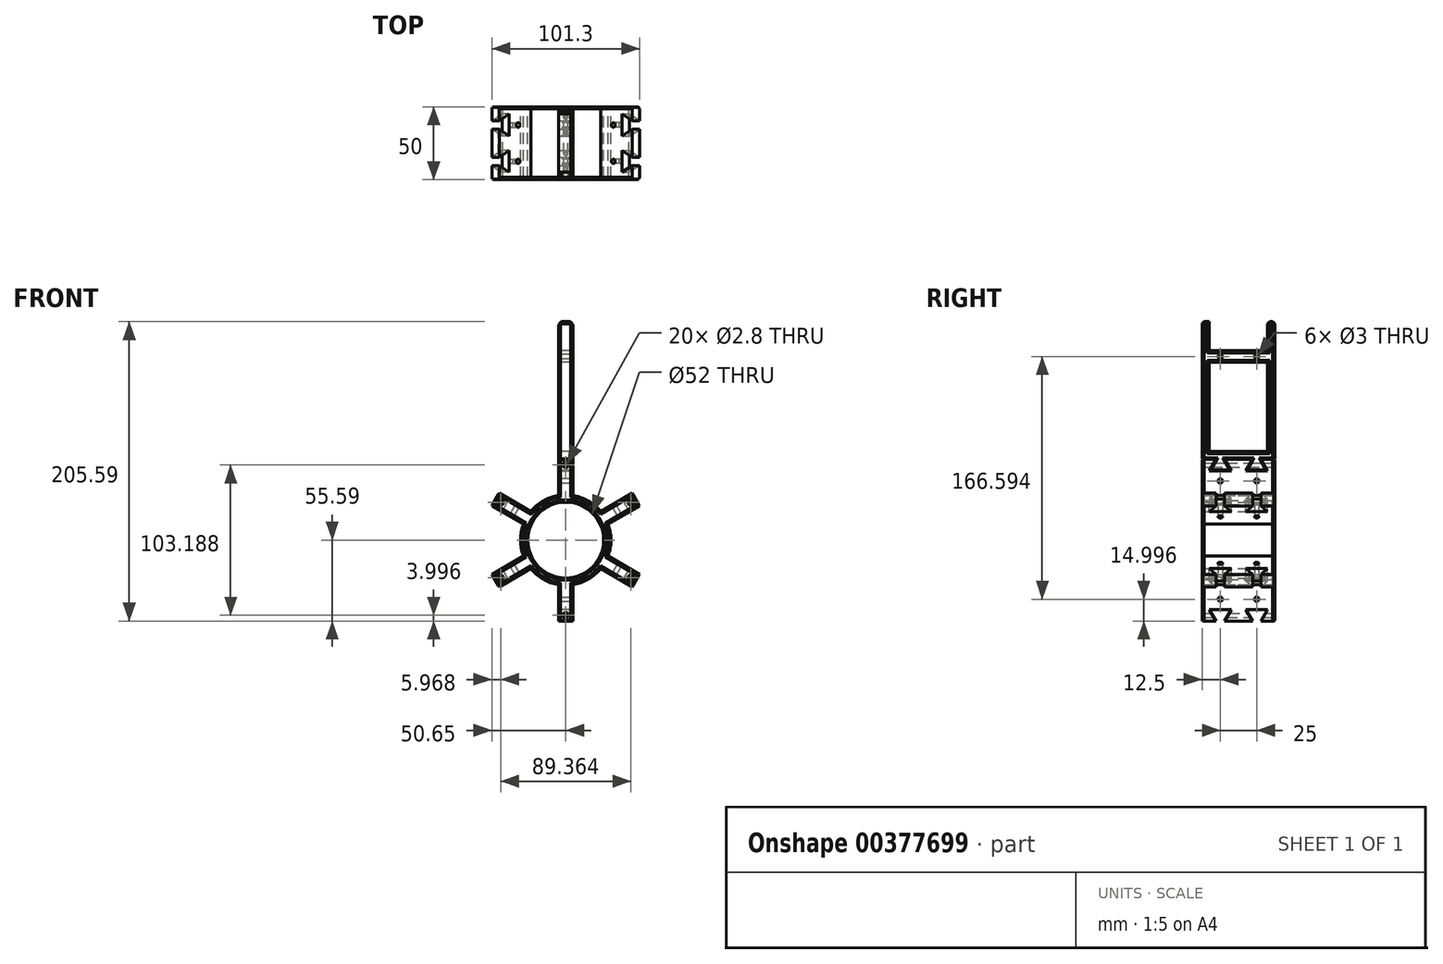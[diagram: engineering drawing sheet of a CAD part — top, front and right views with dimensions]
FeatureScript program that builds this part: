
annotation { "Feature Type Name" : "Feature", "Feature Type Description" : "" }
export const myFeature = defineFeature(function(context is Context, id is Id, definition is map)
    precondition{}
    {
        {
            var Q0;
            Q0=qCreatedBy(makeId("Front.planeOp"),FACE);
            var sketch = newSketch(context, id + "F0", { "sketchPlane" : qUnion([Q0])});
            skCircle(sketch, "E0", {"center": v(0, 0) * mm, "radius": 26 * mm});
            skCircle(sketch, "E1", {"center": v(0, 0) * mm, "radius": 31 * mm});
            skSolve(sketch);
        }
        {
            var Q0;
            Q0=makeQuery(id+"F0.imprint","IMPRINT",FACE,{"disambiguationData":[TD([[makeQuery(id+"F0.imprint","IMPRINT",EDGE,{"derivedFrom":sQuery(id+"F0.wireOp",EDGE,"E0")}),-1.0]])]});
            extrude(context, id + "F1", {"entities" : qUnion([Q0]), "depth" : 50 * mm});
        }
        {
            var Q0;
            Q0=makeQuery(id+"F1.opExtrude","CAP_FACE",FACE,{"disambiguationData":[OSD([sQuery(id+"F0.wireOp",EDGE,"E0"),sQuery(id+"F0.wireOp",EDGE,"E1")])],"isStart":true});
            var sketch = newSketch(context, id + "F2", { "sketchPlane" : qUnion([Q0])});
            skLineSegment(sketch, "E2.bottom", {"start": v(-5, 30.6) * mm, "end": v(5, 30.6) * mm});
            skLineSegment(sketch, "E2.top", {"start": v(-5, 55.6) * mm, "end": v(5, 55.6) * mm});
            skLineSegment(sketch, "E2.left", {"start": v(-5, 30.6) * mm, "end": v(-5, 55.6) * mm});
            skLineSegment(sketch, "E2.right", {"start": v(5, 30.6) * mm, "end": v(5, 55.6) * mm});
            skSolve(sketch);
        }
        {
            var Q0;
            Q0=makeQuery(id+"F2.imprint","IMPRINT",FACE,{"disambiguationData":[TD([[makeQuery(id+"F2.imprint","IMPRINT",EDGE,{"derivedFrom":sQuery(id+"F2.wireOp",EDGE,"E2.top")}),-1.0]])]});
            extrude(context, id + "F3", {"entities" : qUnion([Q0]), "operationType" : NewBodyOperationType.ADD, "oppositeDirection" : true, "depth" : 50 * mm});
        }
        {
            var Q0;
            Q0=makeQuery(id+"F3.opExtrude","SWEPT_FACE",FACE,{"disambiguationData":[OSD([sQuery(id+"F2.wireOp",EDGE,"E2.left")])]});
            var sketch = newSketch(context, id + "F4", { "sketchPlane" : qUnion([Q0])});
            skLineSegment(sketch, "E3", {"start": v(-40.38, 55.6) * mm, "end": v(-45, 47.6) * mm});
            skLineSegment(sketch, "E4", {"start": v(-45, 47.6) * mm, "end": v(-30, 47.6) * mm});
            skLineSegment(sketch, "E5", {"start": v(-30, 47.6) * mm, "end": v(-34.62, 55.6) * mm});
            skLineSegment(sketch, "E6", {"start": v(-9.62, 55.6) * mm, "end": v(-5, 47.6) * mm});
            skLineSegment(sketch, "E7", {"start": v(-5, 47.6) * mm, "end": v(-20, 47.6) * mm});
            skLineSegment(sketch, "E8", {"start": v(-20, 47.6) * mm, "end": v(-15.38, 55.6) * mm});
            skLineSegment(sketch, "E9", {"start": v(-40.38, 55.6) * mm, "end": v(-34.62, 55.6) * mm});
            skLineSegment(sketch, "E10", {"start": v(-15.38, 55.6) * mm, "end": v(-9.62, 55.6) * mm});
            skSolve(sketch);
        }
        {
            var Q0;
            Q0=makeQuery(id+"F4.imprint","IMPRINT",FACE,{"disambiguationData":[TD([[makeQuery(id+"F4.imprint","IMPRINT",EDGE,{"derivedFrom":sQuery(id+"F4.wireOp",EDGE,"E3")}),1.0]])]});
            var Q1;
            Q1=makeQuery(id+"F4.imprint","IMPRINT",FACE,{"disambiguationData":[TD([[makeQuery(id+"F4.imprint","IMPRINT",EDGE,{"derivedFrom":sQuery(id+"F4.wireOp",EDGE,"E6")}),-1.0]])]});
            extrude(context, id + "F5", {"entities" : qUnion([Q0, Q1]), "operationType" : NewBodyOperationType.REMOVE, "oppositeDirection" : true, "depth" : 25 * mm});
        }
        {
            var Q0;
            {var subQ0=sQuery(id+"F0.wireOp",EDGE,"E1");Q0=makeQuery(id+"F3.boolean.opBoolean","MERGE",FACE,{"derivedFrom":[makeQuery(id+"F1.opExtrude","CAP_FACE",FACE,{"disambiguationData":[OSD([sQuery(id+"F0.wireOp",EDGE,"E0"),subQ0])],"isStart":true}),makeQuery(id+"F3.opExtrude","CAP_FACE",FACE,{"disambiguationData":[OSD([subQ0,sQuery(id+"F2.wireOp",EDGE,"E2.top"),sQuery(id+"F2.wireOp",EDGE,"E2.left"),sQuery(id+"F2.wireOp",EDGE,"E2.right")])],"isStart":true})]});}
            var sketch = newSketch(context, id + "F6", { "sketchPlane" : qUnion([Q0])});
            skArc(sketch, "E11.0.0", {"start": v(-5, 30.6) * mm, "mid": v(0, -31) * mm, "end": v(5, 30.6) * mm});
            skLineSegment(sketch, "E11.0.1", {"start": v(5, 30.6) * mm, "end": v(5, 55.6) * mm});
            skLineSegment(sketch, "E11.0.2", {"start": v(5, 55.6) * mm, "end": v(-5, 55.6) * mm});
            skLineSegment(sketch, "E11.0.3", {"start": v(-5, 55.6) * mm, "end": v(-5, 30.6) * mm});
            skCircle(sketch, "E12", {"center": v(0, 51.6) * mm, "radius": 1.4 * mm});
            skSolve(sketch);
        }
        {
            var Q0;
            Q0=makeQuery(id+"F6.imprint","IMPRINT",FACE,{"disambiguationData":[TD([[makeQuery(id+"F6.imprint","IMPRINT",EDGE,{"derivedFrom":sQuery(id+"F6.wireOp",EDGE,"E12")}),1.0]])]});
            extrude(context, id + "F7", {"entities" : qUnion([Q0]), "operationType" : NewBodyOperationType.REMOVE, "endBound" : BoundingType.THROUGH_ALL, "oppositeDirection" : true, "depth" : 25 * mm});
        }
        {
            var Q0;
            Q0=makeQuery(id+"F3.opExtrude","SWEPT_FACE",FACE,{"disambiguationData":[OSD([sQuery(id+"F2.wireOp",EDGE,"E2.right")])]});
            var sketch = newSketch(context, id + "F8", { "sketchPlane" : qUnion([Q0])});
            skCircle(sketch, "E13", {"center": v(12.5, 40.6) * mm, "radius": 1.5 * mm});
            skCircle(sketch, "E14", {"center": v(37.5, 40.6) * mm, "radius": 1.5 * mm});
            skSolve(sketch);
        }
        {
            var Q0;
            Q0=makeQuery(id+"F8.imprint","IMPRINT",FACE,{"disambiguationData":[TD([[makeQuery(id+"F8.imprint","IMPRINT",EDGE,{"derivedFrom":sQuery(id+"F8.wireOp",EDGE,"E13")}),1.0]])]});
            var Q1;
            Q1=makeQuery(id+"F8.imprint","IMPRINT",FACE,{"disambiguationData":[TD([[makeQuery(id+"F8.imprint","IMPRINT",EDGE,{"derivedFrom":sQuery(id+"F8.wireOp",EDGE,"E14")}),1.0]])]});
            extrude(context, id + "F9", {"entities" : qUnion([Q0, Q1]), "operationType" : NewBodyOperationType.REMOVE, "oppositeDirection" : true, "depth" : 25 * mm});
        }
        {
            var Q0;
            Q0=makeQuery(id+"F1.opExtrude","SWEPT_BODY",BODY,{"disambiguationData":[OSD([sQuery(id+"F0.wireOp",EDGE,"E0"),sQuery(id+"F0.wireOp",EDGE,"E1")])]});
            var Q1;
            Q1=makeQuery(id+"F1.opExtrude","CAP_EDGE",EDGE,{"disambiguationData":[OSD([sQuery(id+"F0.wireOp",EDGE,"E0")])],"isStart":false});
            circularPattern(context, id + "F10", {"operationType" : NewBodyOperationType.ADD, "entities" : qUnion([Q0]), "axis" : qUnion([Q1]), "angle" : 360 * degree, "instanceCount" : 6, "equalSpace" : true});
        }
        {
            var Q0;
            Q0=makeQuery(id+"F3.opExtrude","SWEPT_FACE",FACE,{"disambiguationData":[OSD([sQuery(id+"F2.wireOp",EDGE,"E2.right")])]});
            var sketch = newSketch(context, id + "F11", { "sketchPlane" : qUnion([Q0])});
            skLineSegment(sketch, "E15.bottom", {"start": v(0, 55.8) * mm, "end": v(50, 55.8) * mm});
            skLineSegment(sketch, "E15.top", {"start": v(0, 150) * mm, "end": v(50, 150) * mm});
            skLineSegment(sketch, "E15.left", {"start": v(0, 55.8) * mm, "end": v(0, 150) * mm});
            skLineSegment(sketch, "E15.right", {"start": v(50, 55.8) * mm, "end": v(50, 150) * mm});
            skLineSegment(sketch, "E16", {"start": v(9.97, 55.8) * mm, "end": v(5.35, 47.8) * mm});
            skLineSegment(sketch, "E17", {"start": v(5.35, 47.8) * mm, "end": v(19.65, 47.8) * mm});
            skLineSegment(sketch, "E18", {"start": v(19.65, 47.8) * mm, "end": v(15.03, 55.8) * mm});
            skLineSegment(sketch, "E19", {"start": v(34.97, 55.8) * mm, "end": v(30.35, 47.8) * mm});
            skLineSegment(sketch, "E20", {"start": v(30.35, 47.8) * mm, "end": v(44.65, 47.8) * mm});
            skLineSegment(sketch, "E21", {"start": v(44.65, 47.8) * mm, "end": v(40.03, 55.8) * mm});
            skSolve(sketch);
        }
        {
            var Q0;
            Q0=makeQuery(id+"F11.imprint","IMPRINT",FACE,{"disambiguationData":[TD([[makeQuery(id+"F11.imprint","IMPRINT",EDGE,{"derivedFrom":sQuery(id+"F11.wireOp",EDGE,"E15.top")}),-1.0]])]});
            var Q1;
            {var subQ0=sQuery(id+"F11.wireOp",EDGE,"E16");Q1=makeQuery(id+"F11.imprint","IMPRINT",FACE,{"disambiguationData":[TD([[makeQuery(id+"F11.imprint","IMPRINT",EDGE,{"derivedFrom":subQ0}),1.0]])]});}
            var Q2;
            {var subQ0=sQuery(id+"F11.wireOp",EDGE,"E19");Q2=makeQuery(id+"F11.imprint","IMPRINT",FACE,{"disambiguationData":[TD([[makeQuery(id+"F11.imprint","IMPRINT",EDGE,{"derivedFrom":subQ0}),1.0]])]});}
            extrude(context, id + "F12", {"entities" : qUnion([Q0, Q1, Q2]), "oppositeDirection" : true, "depth" : 10 * mm});
        }
        {
            var Q0;
            Q0=makeQuery(id+"F12.opExtrude","CAP_FACE",FACE,{"disambiguationData":[OSD([sQuery(id+"F11.wireOp",EDGE,"E15.bottom"),sQuery(id+"F11.wireOp",EDGE,"E15.top"),sQuery(id+"F11.wireOp",EDGE,"E15.left"),sQuery(id+"F11.wireOp",EDGE,"E15.right"),sQuery(id+"F11.wireOp",EDGE,"E16"),sQuery(id+"F11.wireOp",EDGE,"E17"),sQuery(id+"F11.wireOp",EDGE,"E18"),sQuery(id+"F11.wireOp",EDGE,"E19"),sQuery(id+"F11.wireOp",EDGE,"E20"),sQuery(id+"F11.wireOp",EDGE,"E21")])],"isStart":true});
            var sketch = newSketch(context, id + "F13", { "sketchPlane" : qUnion([Q0])});
            skLineSegment(sketch, "E22.bottom", {"start": v(5, 122) * mm, "end": v(45, 122) * mm});
            skLineSegment(sketch, "E22.top", {"start": v(5, 60.8) * mm, "end": v(45, 60.8) * mm});
            skLineSegment(sketch, "E22.left", {"start": v(5, 122) * mm, "end": v(5, 60.8) * mm});
            skLineSegment(sketch, "E22.right", {"start": v(45, 122) * mm, "end": v(45, 60.8) * mm});
            skLineSegment(sketch, "E23.bottom", {"start": v(5, 150) * mm, "end": v(45, 150) * mm});
            skLineSegment(sketch, "E23.top", {"start": v(5, 130) * mm, "end": v(45, 130) * mm});
            skLineSegment(sketch, "E23.left", {"start": v(5, 150) * mm, "end": v(5, 130) * mm});
            skLineSegment(sketch, "E23.right", {"start": v(45, 150) * mm, "end": v(45, 130) * mm});
            skCircle(sketch, "E24", {"center": v(12.5, 126) * mm, "radius": 1.5 * mm});
            skCircle(sketch, "E25", {"center": v(37.5, 126) * mm, "radius": 1.5 * mm});
            skSolve(sketch);
        }
        {
            var Q0;
            Q0=makeQuery(id+"F13.imprint","IMPRINT",FACE,{"disambiguationData":[TD([[makeQuery(id+"F13.imprint","IMPRINT",EDGE,{"derivedFrom":sQuery(id+"F13.wireOp",EDGE,"E23.bottom")}),-1.0]])]});
            var Q1;
            Q1=makeQuery(id+"F13.imprint","IMPRINT",FACE,{"disambiguationData":[TD([[makeQuery(id+"F13.imprint","IMPRINT",EDGE,{"derivedFrom":sQuery(id+"F13.wireOp",EDGE,"E22.bottom")}),-1.0]])]});
            var Q2;
            Q2=makeQuery(id+"F13.imprint","IMPRINT",FACE,{"disambiguationData":[TD([[makeQuery(id+"F13.imprint","IMPRINT",EDGE,{"derivedFrom":sQuery(id+"F13.wireOp",EDGE,"E24")}),1.0]])]});
            var Q3;
            Q3=makeQuery(id+"F13.imprint","IMPRINT",FACE,{"disambiguationData":[TD([[makeQuery(id+"F13.imprint","IMPRINT",EDGE,{"derivedFrom":sQuery(id+"F13.wireOp",EDGE,"E25")}),1.0]])]});
            extrude(context, id + "F14", {"entities" : qUnion([Q0, Q1, Q2, Q3]), "operationType" : NewBodyOperationType.REMOVE, "oppositeDirection" : true, "depth" : 25 * mm});
        }
        {
            var Q0;
            Q0=makeQuery(id+"F12.opExtrude","SWEPT_FACE",FACE,{"disambiguationData":[OSD([sQuery(id+"F11.wireOp",EDGE,"E15.left")])]});
            var sketch = newSketch(context, id + "F15", { "sketchPlane" : qUnion([Q0])});
            skCircle(sketch, "E26.0", {"center": v(0, 51.6) * mm, "radius": 1.4 * mm});
            skSolve(sketch);
        }
        {
            var Q0;
            Q0=makeQuery(id+"F15.imprint","IMPRINT",FACE,{"disambiguationData":[TD([[makeQuery(id+"F15.imprint","IMPRINT",EDGE,{"derivedFrom":sQuery(id+"F15.wireOp",EDGE,"E26.0")}),1.0]])]});
            extrude(context, id + "F16", {"entities" : qUnion([Q0]), "operationType" : NewBodyOperationType.REMOVE, "endBound" : BoundingType.THROUGH_ALL, "oppositeDirection" : true, "depth" : 25 * mm});
        }
        {
            assignVariable(context, id + "F17", {"name" : "c", "anyValue" : 1.5});
        }
        {
            var Q0;
            {var subQ0=sQuery(id+"F2.wireOp",EDGE,"E2.right");var subQ2=sQuery(id+"F0.wireOp",EDGE,"E1");Q0=makeQuery(id+"F10.boolean.opBoolean","SPLIT",EDGE,{"disambiguationData":[TD([makeQuery(id+"F3.opExtrude","SWEPT_FACE",FACE,{"disambiguationData":[OSD([subQ0])]})])],"derivedFrom":makeQuery(id+"F1.opExtrude","CAP_EDGE",EDGE,{"disambiguationData":[OSD([subQ2])],"isStart":false})});}
            var Q1;
            Q1=makeQuery(id+"F3.opExtrude","CAP_EDGE",EDGE,{"disambiguationData":[OSD([sQuery(id+"F2.wireOp",EDGE,"E2.right")])],"isStart":false});
            var Q2;
            Q2=makeQuery(id+"F3.opExtrude","CAP_EDGE",EDGE,{"disambiguationData":[OSD([sQuery(id+"F2.wireOp",EDGE,"E2.left")])],"isStart":false});
            var Q3;
            {var subQ0=sQuery(id+"F2.wireOp",EDGE,"E2.left");var subQ2=sQuery(id+"F0.wireOp",EDGE,"E1");Q3=makeQuery(id+"F10.boolean.opBoolean","SPLIT",EDGE,{"disambiguationData":[TD([makeQuery(id+"F3.opExtrude","SWEPT_FACE",FACE,{"disambiguationData":[OSD([subQ0])]})])],"derivedFrom":makeQuery(id+"F1.opExtrude","CAP_EDGE",EDGE,{"disambiguationData":[OSD([subQ2])],"isStart":false})});}
            var Q4;
            Q4=makeQuery(id+"F10.opPattern","COPY",EDGE,{"derivedFrom":makeQuery(id+"F3.opExtrude","CAP_EDGE",EDGE,{"disambiguationData":[OSD([sQuery(id+"F2.wireOp",EDGE,"E2.right")])],"isStart":false}),"instanceName":"5"});
            var Q5;
            Q5=makeQuery(id+"F10.opPattern","COPY",EDGE,{"derivedFrom":makeQuery(id+"F3.opExtrude","CAP_EDGE",EDGE,{"disambiguationData":[OSD([sQuery(id+"F2.wireOp",EDGE,"E2.left")])],"isStart":false}),"instanceName":"5"});
            var Q6;
            {var subQ0=sQuery(id+"F2.wireOp",EDGE,"E2.right");var subQ2=sQuery(id+"F0.wireOp",EDGE,"E1");Q6=makeQuery(id+"F10.boolean.opBoolean","SPLIT",EDGE,{"disambiguationData":[TD([makeQuery(id+"F10.opPattern","COPY",FACE,{"derivedFrom":makeQuery(id+"F3.opExtrude","SWEPT_FACE",FACE,{"disambiguationData":[OSD([subQ0])]}),"instanceName":"4"})])],"derivedFrom":makeQuery(id+"F1.opExtrude","CAP_EDGE",EDGE,{"disambiguationData":[OSD([subQ2])],"isStart":false})});}
            var Q7;
            Q7=makeQuery(id+"F10.opPattern","COPY",EDGE,{"derivedFrom":makeQuery(id+"F3.opExtrude","CAP_EDGE",EDGE,{"disambiguationData":[OSD([sQuery(id+"F2.wireOp",EDGE,"E2.right")])],"isStart":false}),"instanceName":"4"});
            var Q8;
            Q8=makeQuery(id+"F10.opPattern","COPY",EDGE,{"derivedFrom":makeQuery(id+"F3.opExtrude","CAP_EDGE",EDGE,{"disambiguationData":[OSD([sQuery(id+"F2.wireOp",EDGE,"E2.left")])],"isStart":false}),"instanceName":"4"});
            var Q9;
            {var subQ0=sQuery(id+"F2.wireOp",EDGE,"E2.right");var subQ2=sQuery(id+"F0.wireOp",EDGE,"E1");Q9=makeQuery(id+"F10.boolean.opBoolean","SPLIT",EDGE,{"disambiguationData":[TD([makeQuery(id+"F10.opPattern","COPY",FACE,{"derivedFrom":makeQuery(id+"F3.opExtrude","SWEPT_FACE",FACE,{"disambiguationData":[OSD([subQ0])]}),"instanceName":"3"})])],"derivedFrom":makeQuery(id+"F1.opExtrude","CAP_EDGE",EDGE,{"disambiguationData":[OSD([subQ2])],"isStart":false})});}
            var Q10;
            Q10=makeQuery(id+"F10.opPattern","COPY",EDGE,{"derivedFrom":makeQuery(id+"F3.opExtrude","CAP_EDGE",EDGE,{"disambiguationData":[OSD([sQuery(id+"F2.wireOp",EDGE,"E2.right")])],"isStart":false}),"instanceName":"3"});
            var Q11;
            Q11=makeQuery(id+"F10.opPattern","COPY",EDGE,{"derivedFrom":makeQuery(id+"F3.opExtrude","CAP_EDGE",EDGE,{"disambiguationData":[OSD([sQuery(id+"F2.wireOp",EDGE,"E2.left")])],"isStart":false}),"instanceName":"3"});
            var Q12;
            {var subQ0=sQuery(id+"F2.wireOp",EDGE,"E2.right");var subQ2=sQuery(id+"F0.wireOp",EDGE,"E1");Q12=makeQuery(id+"F10.boolean.opBoolean","SPLIT",EDGE,{"disambiguationData":[TD([makeQuery(id+"F10.opPattern","COPY",FACE,{"derivedFrom":makeQuery(id+"F3.opExtrude","SWEPT_FACE",FACE,{"disambiguationData":[OSD([subQ0])]}),"instanceName":"2"})])],"derivedFrom":makeQuery(id+"F1.opExtrude","CAP_EDGE",EDGE,{"disambiguationData":[OSD([subQ2])],"isStart":false})});}
            var Q13;
            Q13=makeQuery(id+"F10.opPattern","COPY",EDGE,{"derivedFrom":makeQuery(id+"F3.opExtrude","CAP_EDGE",EDGE,{"disambiguationData":[OSD([sQuery(id+"F2.wireOp",EDGE,"E2.right")])],"isStart":false}),"instanceName":"2"});
            var Q14;
            Q14=makeQuery(id+"F10.opPattern","COPY",EDGE,{"derivedFrom":makeQuery(id+"F3.opExtrude","CAP_EDGE",EDGE,{"disambiguationData":[OSD([sQuery(id+"F2.wireOp",EDGE,"E2.left")])],"isStart":false}),"instanceName":"2"});
            var Q15;
            {var subQ0=sQuery(id+"F2.wireOp",EDGE,"E2.right");var subQ2=sQuery(id+"F0.wireOp",EDGE,"E1");Q15=makeQuery(id+"F10.boolean.opBoolean","SPLIT",EDGE,{"disambiguationData":[TD([makeQuery(id+"F10.opPattern","COPY",FACE,{"derivedFrom":makeQuery(id+"F3.opExtrude","SWEPT_FACE",FACE,{"disambiguationData":[OSD([subQ0])]}),"instanceName":"1"})])],"derivedFrom":makeQuery(id+"F1.opExtrude","CAP_EDGE",EDGE,{"disambiguationData":[OSD([subQ2])],"isStart":false})});}
            var Q16;
            Q16=makeQuery(id+"F10.opPattern","COPY",EDGE,{"derivedFrom":makeQuery(id+"F3.opExtrude","CAP_EDGE",EDGE,{"disambiguationData":[OSD([sQuery(id+"F2.wireOp",EDGE,"E2.right")])],"isStart":false}),"instanceName":"1"});
            var Q17;
            Q17=makeQuery(id+"F10.opPattern","COPY",EDGE,{"derivedFrom":makeQuery(id+"F3.opExtrude","CAP_EDGE",EDGE,{"disambiguationData":[OSD([sQuery(id+"F2.wireOp",EDGE,"E2.left")])],"isStart":false}),"instanceName":"1"});
            var Q18;
            Q18=makeQuery(id+"F1.opExtrude","CAP_EDGE",EDGE,{"disambiguationData":[OSD([sQuery(id+"F0.wireOp",EDGE,"E0")])],"isStart":false});
            chamfer(context, id + "F18", {"entities" : qUnion([Q0, Q1, Q2, Q3, Q4, Q5, Q6, Q7, Q8, Q9, Q10, Q11, Q12, Q13, Q14, Q15, Q16, Q17, Q18]), "width" : (getVariable(context, 'c')) * mm, "tangentPropagation" : true});
        }
        {
            var Q0;
            Q0=makeQuery(id+"F10.opPattern","COPY",EDGE,{"derivedFrom":makeQuery(id+"F3.opExtrude","CAP_EDGE",EDGE,{"disambiguationData":[OSD([sQuery(id+"F2.wireOp",EDGE,"E2.right")])],"isStart":true}),"instanceName":"5"});
            var Q1;
            {var subQ1=sQuery(id+"F2.wireOp",EDGE,"E2.left");var subQ2=sQuery(id+"F0.wireOp",EDGE,"E1");Q1=makeQuery(id+"F10.boolean.opBoolean","SPLIT",EDGE,{"disambiguationData":[TD([makeQuery(id+"F3.opExtrude","SWEPT_FACE",FACE,{"disambiguationData":[OSD([subQ1])]})])],"derivedFrom":makeQuery(id+"F1.opExtrude","CAP_EDGE",EDGE,{"disambiguationData":[OSD([subQ2])],"isStart":true})});}
            var Q2;
            Q2=makeQuery(id+"F3.opExtrude","CAP_EDGE",EDGE,{"disambiguationData":[OSD([sQuery(id+"F2.wireOp",EDGE,"E2.left")])],"isStart":true});
            var Q3;
            Q3=makeQuery(id+"F3.opExtrude","CAP_EDGE",EDGE,{"disambiguationData":[OSD([sQuery(id+"F2.wireOp",EDGE,"E2.right")])],"isStart":true});
            var Q4;
            {var subQ0=sQuery(id+"F2.wireOp",EDGE,"E2.right");var subQ2=sQuery(id+"F0.wireOp",EDGE,"E1");Q4=makeQuery(id+"F10.boolean.opBoolean","SPLIT",EDGE,{"disambiguationData":[TD([makeQuery(id+"F3.opExtrude","SWEPT_FACE",FACE,{"disambiguationData":[OSD([subQ0])]})])],"derivedFrom":makeQuery(id+"F1.opExtrude","CAP_EDGE",EDGE,{"disambiguationData":[OSD([subQ2])],"isStart":true})});}
            var Q5;
            Q5=makeQuery(id+"F10.opPattern","COPY",EDGE,{"derivedFrom":makeQuery(id+"F3.opExtrude","CAP_EDGE",EDGE,{"disambiguationData":[OSD([sQuery(id+"F2.wireOp",EDGE,"E2.left")])],"isStart":true}),"instanceName":"1"});
            var Q6;
            Q6=makeQuery(id+"F10.opPattern","COPY",EDGE,{"derivedFrom":makeQuery(id+"F3.opExtrude","CAP_EDGE",EDGE,{"disambiguationData":[OSD([sQuery(id+"F2.wireOp",EDGE,"E2.right")])],"isStart":true}),"instanceName":"1"});
            var Q7;
            {var subQ0=sQuery(id+"F2.wireOp",EDGE,"E2.right");var subQ2=sQuery(id+"F0.wireOp",EDGE,"E1");Q7=makeQuery(id+"F10.boolean.opBoolean","SPLIT",EDGE,{"disambiguationData":[TD([makeQuery(id+"F10.opPattern","COPY",FACE,{"derivedFrom":makeQuery(id+"F3.opExtrude","SWEPT_FACE",FACE,{"disambiguationData":[OSD([subQ0])]}),"instanceName":"1"})])],"derivedFrom":makeQuery(id+"F1.opExtrude","CAP_EDGE",EDGE,{"disambiguationData":[OSD([subQ2])],"isStart":true})});}
            var Q8;
            Q8=makeQuery(id+"F10.opPattern","COPY",EDGE,{"derivedFrom":makeQuery(id+"F3.opExtrude","CAP_EDGE",EDGE,{"disambiguationData":[OSD([sQuery(id+"F2.wireOp",EDGE,"E2.left")])],"isStart":true}),"instanceName":"2"});
            var Q9;
            Q9=makeQuery(id+"F10.opPattern","COPY",EDGE,{"derivedFrom":makeQuery(id+"F3.opExtrude","CAP_EDGE",EDGE,{"disambiguationData":[OSD([sQuery(id+"F2.wireOp",EDGE,"E2.right")])],"isStart":true}),"instanceName":"2"});
            var Q10;
            Q10=makeQuery(id+"F10.opPattern","COPY",EDGE,{"derivedFrom":makeQuery(id+"F3.opExtrude","CAP_EDGE",EDGE,{"disambiguationData":[OSD([sQuery(id+"F2.wireOp",EDGE,"E2.left")])],"isStart":true}),"instanceName":"3"});
            var Q11;
            {var subQ0=sQuery(id+"F2.wireOp",EDGE,"E2.right");var subQ2=sQuery(id+"F0.wireOp",EDGE,"E1");Q11=makeQuery(id+"F10.boolean.opBoolean","SPLIT",EDGE,{"disambiguationData":[TD([makeQuery(id+"F10.opPattern","COPY",FACE,{"derivedFrom":makeQuery(id+"F3.opExtrude","SWEPT_FACE",FACE,{"disambiguationData":[OSD([subQ0])]}),"instanceName":"2"})])],"derivedFrom":makeQuery(id+"F1.opExtrude","CAP_EDGE",EDGE,{"disambiguationData":[OSD([subQ2])],"isStart":true})});}
            var Q12;
            Q12=makeQuery(id+"F10.opPattern","COPY",EDGE,{"derivedFrom":makeQuery(id+"F3.opExtrude","CAP_EDGE",EDGE,{"disambiguationData":[OSD([sQuery(id+"F2.wireOp",EDGE,"E2.right")])],"isStart":true}),"instanceName":"3"});
            var Q13;
            {var subQ0=sQuery(id+"F2.wireOp",EDGE,"E2.right");var subQ2=sQuery(id+"F0.wireOp",EDGE,"E1");Q13=makeQuery(id+"F10.boolean.opBoolean","SPLIT",EDGE,{"disambiguationData":[TD([makeQuery(id+"F10.opPattern","COPY",FACE,{"derivedFrom":makeQuery(id+"F3.opExtrude","SWEPT_FACE",FACE,{"disambiguationData":[OSD([subQ0])]}),"instanceName":"3"})])],"derivedFrom":makeQuery(id+"F1.opExtrude","CAP_EDGE",EDGE,{"disambiguationData":[OSD([subQ2])],"isStart":true})});}
            var Q14;
            Q14=makeQuery(id+"F10.opPattern","COPY",EDGE,{"derivedFrom":makeQuery(id+"F3.opExtrude","CAP_EDGE",EDGE,{"disambiguationData":[OSD([sQuery(id+"F2.wireOp",EDGE,"E2.left")])],"isStart":true}),"instanceName":"4"});
            var Q15;
            Q15=makeQuery(id+"F10.opPattern","COPY",EDGE,{"derivedFrom":makeQuery(id+"F3.opExtrude","CAP_EDGE",EDGE,{"disambiguationData":[OSD([sQuery(id+"F2.wireOp",EDGE,"E2.right")])],"isStart":true}),"instanceName":"4"});
            var Q16;
            {var subQ0=sQuery(id+"F2.wireOp",EDGE,"E2.right");var subQ2=sQuery(id+"F0.wireOp",EDGE,"E1");Q16=makeQuery(id+"F10.boolean.opBoolean","SPLIT",EDGE,{"disambiguationData":[TD([makeQuery(id+"F10.opPattern","COPY",FACE,{"derivedFrom":makeQuery(id+"F3.opExtrude","SWEPT_FACE",FACE,{"disambiguationData":[OSD([subQ0])]}),"instanceName":"4"})])],"derivedFrom":makeQuery(id+"F1.opExtrude","CAP_EDGE",EDGE,{"disambiguationData":[OSD([subQ2])],"isStart":true})});}
            var Q17;
            Q17=makeQuery(id+"F10.opPattern","COPY",EDGE,{"derivedFrom":makeQuery(id+"F3.opExtrude","CAP_EDGE",EDGE,{"disambiguationData":[OSD([sQuery(id+"F2.wireOp",EDGE,"E2.left")])],"isStart":true}),"instanceName":"5"});
            var Q18;
            Q18=makeQuery(id+"F1.opExtrude","CAP_EDGE",EDGE,{"disambiguationData":[OSD([sQuery(id+"F0.wireOp",EDGE,"E0")])],"isStart":true});
            chamfer(context, id + "F19", {"entities" : qUnion([Q0, Q1, Q2, Q3, Q4, Q5, Q6, Q7, Q8, Q9, Q10, Q11, Q12, Q13, Q14, Q15, Q16, Q17, Q18]), "width" : (getVariable(context, 'c')) * mm, "tangentPropagation" : true});
        }
        {
            var Q0;
            Q0=makeQuery(id+"F12.opExtrude","CAP_EDGE",EDGE,{"disambiguationData":[OSD([sQuery(id+"F11.wireOp",EDGE,"E15.left")])],"isStart":true});
            var Q1;
            Q1=makeQuery(id+"F14.boolean.opBoolean","COPY",EDGE,{"derivedFrom":makeQuery(id+"F14.opExtrude","CAP_EDGE",EDGE,{"disambiguationData":[OSD([sQuery(id+"F13.wireOp",EDGE,"E22.left")])],"isStart":true})});
            var Q2;
            Q2=makeQuery(id+"F14.boolean.opBoolean","COPY",EDGE,{"derivedFrom":makeQuery(id+"F14.opExtrude","CAP_EDGE",EDGE,{"disambiguationData":[OSD([sQuery(id+"F13.wireOp",EDGE,"E22.bottom")])],"isStart":true})});
            var Q3;
            Q3=makeQuery(id+"F14.boolean.opBoolean","COPY",EDGE,{"derivedFrom":makeQuery(id+"F14.opExtrude","CAP_EDGE",EDGE,{"disambiguationData":[OSD([sQuery(id+"F13.wireOp",EDGE,"E22.right")])],"isStart":true})});
            var Q4;
            Q4=makeQuery(id+"F14.boolean.opBoolean","COPY",EDGE,{"derivedFrom":makeQuery(id+"F14.opExtrude","CAP_EDGE",EDGE,{"disambiguationData":[OSD([sQuery(id+"F13.wireOp",EDGE,"E22.top")])],"isStart":true})});
            var Q5;
            Q5=makeQuery(id+"F14.boolean.opBoolean","COPY",EDGE,{"derivedFrom":makeQuery(id+"F14.opExtrude","CAP_EDGE",EDGE,{"disambiguationData":[OSD([sQuery(id+"F13.wireOp",EDGE,"E23.top")])],"isStart":true})});
            var Q6;
            Q6=makeQuery(id+"F14.boolean.opBoolean","COPY",EDGE,{"derivedFrom":makeQuery(id+"F14.opExtrude","CAP_EDGE",EDGE,{"disambiguationData":[OSD([sQuery(id+"F13.wireOp",EDGE,"E23.left")])],"isStart":true})});
            var Q7;
            Q7=makeQuery(id+"F14.boolean.opBoolean","COPY",EDGE,{"derivedFrom":makeQuery(id+"F14.opExtrude","CAP_EDGE",EDGE,{"disambiguationData":[OSD([sQuery(id+"F13.wireOp",EDGE,"E23.right")])],"isStart":true})});
            var Q8;
            Q8=makeQuery(id+"F12.opExtrude","CAP_EDGE",EDGE,{"disambiguationData":[OSD([sQuery(id+"F11.wireOp",EDGE,"E15.right")])],"isStart":false});
            var Q9;
            Q9=makeQuery(id+"F12.opExtrude","CAP_EDGE",EDGE,{"disambiguationData":[OSD([sQuery(id+"F11.wireOp",EDGE,"E15.right")])],"isStart":true});
            var Q10;
            Q10=makeQuery(id+"F14.boolean.opBoolean","INTERSECT",EDGE,{"derivedFrom":[makeQuery(id+"F12.opExtrude","CAP_FACE",FACE,{"disambiguationData":[OSD([sQuery(id+"F11.wireOp",EDGE,"E15.bottom"),sQuery(id+"F11.wireOp",EDGE,"E15.top"),sQuery(id+"F11.wireOp",EDGE,"E15.left"),sQuery(id+"F11.wireOp",EDGE,"E15.right"),sQuery(id+"F11.wireOp",EDGE,"E16"),sQuery(id+"F11.wireOp",EDGE,"E17"),sQuery(id+"F11.wireOp",EDGE,"E18"),sQuery(id+"F11.wireOp",EDGE,"E19"),sQuery(id+"F11.wireOp",EDGE,"E20"),sQuery(id+"F11.wireOp",EDGE,"E21")])],"isStart":false}),makeQuery(id+"F14.opExtrude","SWEPT_FACE",FACE,{"disambiguationData":[OSD([sQuery(id+"F13.wireOp",EDGE,"E22.bottom")])]})]});
            var Q11;
            Q11=makeQuery(id+"F14.boolean.opBoolean","INTERSECT",EDGE,{"derivedFrom":[makeQuery(id+"F12.opExtrude","CAP_FACE",FACE,{"disambiguationData":[OSD([sQuery(id+"F11.wireOp",EDGE,"E15.bottom"),sQuery(id+"F11.wireOp",EDGE,"E15.top"),sQuery(id+"F11.wireOp",EDGE,"E15.left"),sQuery(id+"F11.wireOp",EDGE,"E15.right"),sQuery(id+"F11.wireOp",EDGE,"E16"),sQuery(id+"F11.wireOp",EDGE,"E17"),sQuery(id+"F11.wireOp",EDGE,"E18"),sQuery(id+"F11.wireOp",EDGE,"E19"),sQuery(id+"F11.wireOp",EDGE,"E20"),sQuery(id+"F11.wireOp",EDGE,"E21")])],"isStart":false}),makeQuery(id+"F14.opExtrude","SWEPT_FACE",FACE,{"disambiguationData":[OSD([sQuery(id+"F13.wireOp",EDGE,"E22.right")])]})]});
            var Q12;
            Q12=makeQuery(id+"F14.boolean.opBoolean","INTERSECT",EDGE,{"derivedFrom":[makeQuery(id+"F12.opExtrude","CAP_FACE",FACE,{"disambiguationData":[OSD([sQuery(id+"F11.wireOp",EDGE,"E15.bottom"),sQuery(id+"F11.wireOp",EDGE,"E15.top"),sQuery(id+"F11.wireOp",EDGE,"E15.left"),sQuery(id+"F11.wireOp",EDGE,"E15.right"),sQuery(id+"F11.wireOp",EDGE,"E16"),sQuery(id+"F11.wireOp",EDGE,"E17"),sQuery(id+"F11.wireOp",EDGE,"E18"),sQuery(id+"F11.wireOp",EDGE,"E19"),sQuery(id+"F11.wireOp",EDGE,"E20"),sQuery(id+"F11.wireOp",EDGE,"E21")])],"isStart":false}),makeQuery(id+"F14.opExtrude","SWEPT_FACE",FACE,{"disambiguationData":[OSD([sQuery(id+"F13.wireOp",EDGE,"E22.top")])]})]});
            var Q13;
            Q13=makeQuery(id+"F12.opExtrude","CAP_EDGE",EDGE,{"disambiguationData":[OSD([sQuery(id+"F11.wireOp",EDGE,"E15.left")])],"isStart":false});
            var Q14;
            Q14=makeQuery(id+"F14.boolean.opBoolean","INTERSECT",EDGE,{"derivedFrom":[makeQuery(id+"F12.opExtrude","CAP_FACE",FACE,{"disambiguationData":[OSD([sQuery(id+"F11.wireOp",EDGE,"E15.bottom"),sQuery(id+"F11.wireOp",EDGE,"E15.top"),sQuery(id+"F11.wireOp",EDGE,"E15.left"),sQuery(id+"F11.wireOp",EDGE,"E15.right"),sQuery(id+"F11.wireOp",EDGE,"E16"),sQuery(id+"F11.wireOp",EDGE,"E17"),sQuery(id+"F11.wireOp",EDGE,"E18"),sQuery(id+"F11.wireOp",EDGE,"E19"),sQuery(id+"F11.wireOp",EDGE,"E20"),sQuery(id+"F11.wireOp",EDGE,"E21")])],"isStart":false}),makeQuery(id+"F14.opExtrude","SWEPT_FACE",FACE,{"disambiguationData":[OSD([sQuery(id+"F13.wireOp",EDGE,"E22.left")])]})]});
            var Q15;
            Q15=makeQuery(id+"F14.boolean.opBoolean","INTERSECT",EDGE,{"derivedFrom":[makeQuery(id+"F12.opExtrude","CAP_FACE",FACE,{"disambiguationData":[OSD([sQuery(id+"F11.wireOp",EDGE,"E15.bottom"),sQuery(id+"F11.wireOp",EDGE,"E15.top"),sQuery(id+"F11.wireOp",EDGE,"E15.left"),sQuery(id+"F11.wireOp",EDGE,"E15.right"),sQuery(id+"F11.wireOp",EDGE,"E16"),sQuery(id+"F11.wireOp",EDGE,"E17"),sQuery(id+"F11.wireOp",EDGE,"E18"),sQuery(id+"F11.wireOp",EDGE,"E19"),sQuery(id+"F11.wireOp",EDGE,"E20"),sQuery(id+"F11.wireOp",EDGE,"E21")])],"isStart":false}),makeQuery(id+"F14.opExtrude","SWEPT_FACE",FACE,{"disambiguationData":[OSD([sQuery(id+"F13.wireOp",EDGE,"E23.top")])]})]});
            var Q16;
            Q16=makeQuery(id+"F14.boolean.opBoolean","INTERSECT",EDGE,{"derivedFrom":[makeQuery(id+"F12.opExtrude","CAP_FACE",FACE,{"disambiguationData":[OSD([sQuery(id+"F11.wireOp",EDGE,"E15.bottom"),sQuery(id+"F11.wireOp",EDGE,"E15.top"),sQuery(id+"F11.wireOp",EDGE,"E15.left"),sQuery(id+"F11.wireOp",EDGE,"E15.right"),sQuery(id+"F11.wireOp",EDGE,"E16"),sQuery(id+"F11.wireOp",EDGE,"E17"),sQuery(id+"F11.wireOp",EDGE,"E18"),sQuery(id+"F11.wireOp",EDGE,"E19"),sQuery(id+"F11.wireOp",EDGE,"E20"),sQuery(id+"F11.wireOp",EDGE,"E21")])],"isStart":false}),makeQuery(id+"F14.opExtrude","SWEPT_FACE",FACE,{"disambiguationData":[OSD([sQuery(id+"F13.wireOp",EDGE,"E23.right")])]})]});
            var Q17;
            Q17=makeQuery(id+"F14.boolean.opBoolean","INTERSECT",EDGE,{"derivedFrom":[makeQuery(id+"F12.opExtrude","CAP_FACE",FACE,{"disambiguationData":[OSD([sQuery(id+"F11.wireOp",EDGE,"E15.bottom"),sQuery(id+"F11.wireOp",EDGE,"E15.top"),sQuery(id+"F11.wireOp",EDGE,"E15.left"),sQuery(id+"F11.wireOp",EDGE,"E15.right"),sQuery(id+"F11.wireOp",EDGE,"E16"),sQuery(id+"F11.wireOp",EDGE,"E17"),sQuery(id+"F11.wireOp",EDGE,"E18"),sQuery(id+"F11.wireOp",EDGE,"E19"),sQuery(id+"F11.wireOp",EDGE,"E20"),sQuery(id+"F11.wireOp",EDGE,"E21")])],"isStart":false}),makeQuery(id+"F14.opExtrude","SWEPT_FACE",FACE,{"disambiguationData":[OSD([sQuery(id+"F13.wireOp",EDGE,"E23.left")])]})]});
            chamfer(context, id + "F20", {"entities" : qUnion([Q0, Q1, Q2, Q3, Q4, Q5, Q6, Q7, Q8, Q9, Q10, Q11, Q12, Q13, Q14, Q15, Q16, Q17]), "width" : (getVariable(context, 'c')) * mm, "tangentPropagation" : true});
        }
        {
            var Q0;
            Q0=makeQuery(id+"F12.opExtrude","SWEPT_EDGE",EDGE,{"disambiguationData":[OSD([sQuery(id+"F11.wireOp",EDGE,"E15.top"),sQuery(id+"F11.wireOp",EDGE,"E15.left")])]});
            var Q1;
            Q1=makeQuery(id+"F14.boolean.opBoolean","COPY",EDGE,{"derivedFrom":makeQuery(id+"F14.opExtrude","SWEPT_EDGE",EDGE,{"disambiguationData":[OSD([sQuery(id+"F11.wireOp",EDGE,"E15.top"),sQuery(id+"F13.wireOp",EDGE,"E23.bottom"),sQuery(id+"F13.wireOp",EDGE,"E23.left")])]})});
            var Q2;
            Q2=makeQuery(id+"F14.boolean.opBoolean","COPY",EDGE,{"derivedFrom":makeQuery(id+"F14.opExtrude","SWEPT_EDGE",EDGE,{"disambiguationData":[OSD([sQuery(id+"F11.wireOp",EDGE,"E15.top"),sQuery(id+"F13.wireOp",EDGE,"E23.bottom"),sQuery(id+"F13.wireOp",EDGE,"E23.right")])]})});
            var Q3;
            Q3=makeQuery(id+"F12.opExtrude","SWEPT_EDGE",EDGE,{"disambiguationData":[OSD([sQuery(id+"F11.wireOp",EDGE,"E15.top"),sQuery(id+"F11.wireOp",EDGE,"E15.right")])]});
            chamfer(context, id + "F21", {"entities" : qUnion([Q0, Q1, Q2, Q3]), "width" : (getVariable(context, 'c')) * mm, "tangentPropagation" : true});
        }
        {
            assignVariable(context, id + "F22", {"name" : "c2", "anyValue" : 0.5});
        }
        {
            var Q0;
            Q0=makeQuery(id+"F12.opExtrude","CAP_EDGE",EDGE,{"disambiguationData":[OSD([sQuery(id+"F11.wireOp",EDGE,"E16")])],"isStart":true});
            var Q1;
            Q1=makeQuery(id+"F12.opExtrude","CAP_EDGE",EDGE,{"disambiguationData":[OSD([sQuery(id+"F11.wireOp",EDGE,"E17")])],"isStart":true});
            var Q2;
            Q2=makeQuery(id+"F12.opExtrude","CAP_EDGE",EDGE,{"disambiguationData":[OSD([sQuery(id+"F11.wireOp",EDGE,"E18")])],"isStart":true});
            var Q3;
            {var subQ0=sQuery(id+"F11.wireOp",EDGE,"E15.bottom");Q3=makeQuery(id+"F12.opExtrude","CAP_EDGE",EDGE,{"disambiguationData":[OSD([subQ0]),TDD([makeQuery(id+"F11.imprint","IMPRINT",EDGE,{"disambiguationData":[TD([[makeQuery(id+"F11.imprint","INTERSECT",VERTEX,{"derivedFrom":[subQ0,sQuery(id+"F11.wireOp",EDGE,"E18")]}),-1.0]])],"derivedFrom":subQ0})])],"isStart":true});}
            var Q4;
            {var subQ0=sQuery(id+"F11.wireOp",EDGE,"E15.bottom");Q4=makeQuery(id+"F12.opExtrude","CAP_EDGE",EDGE,{"disambiguationData":[OSD([subQ0]),TDD([makeQuery(id+"F11.imprint","IMPRINT",EDGE,{"disambiguationData":[TD([[makeQuery(id+"F11.imprint","INTERSECT",VERTEX,{"derivedFrom":[subQ0,sQuery(id+"F11.wireOp",EDGE,"E15.left")]}),-1.0]])],"derivedFrom":subQ0})])],"isStart":true});}
            var Q5;
            {var subQ0=sQuery(id+"F11.wireOp",EDGE,"E15.bottom");Q5=makeQuery(id+"F12.opExtrude","CAP_EDGE",EDGE,{"disambiguationData":[OSD([subQ0]),TDD([makeQuery(id+"F11.imprint","IMPRINT",EDGE,{"disambiguationData":[TD([[makeQuery(id+"F11.imprint","INTERSECT",VERTEX,{"derivedFrom":[subQ0,sQuery(id+"F11.wireOp",EDGE,"E15.right")]}),1.0]])],"derivedFrom":subQ0})])],"isStart":true});}
            var Q6;
            Q6=makeQuery(id+"F12.opExtrude","CAP_EDGE",EDGE,{"disambiguationData":[OSD([sQuery(id+"F11.wireOp",EDGE,"E21")])],"isStart":true});
            var Q7;
            Q7=makeQuery(id+"F12.opExtrude","CAP_EDGE",EDGE,{"disambiguationData":[OSD([sQuery(id+"F11.wireOp",EDGE,"E20")])],"isStart":true});
            var Q8;
            Q8=makeQuery(id+"F12.opExtrude","CAP_EDGE",EDGE,{"disambiguationData":[OSD([sQuery(id+"F11.wireOp",EDGE,"E19")])],"isStart":true});
            var Q9;
            {var subQ0=sQuery(id+"F11.wireOp",EDGE,"E15.bottom");Q9=makeQuery(id+"F12.opExtrude","CAP_EDGE",EDGE,{"disambiguationData":[OSD([subQ0]),TDD([makeQuery(id+"F11.imprint","IMPRINT",EDGE,{"disambiguationData":[TD([[makeQuery(id+"F11.imprint","INTERSECT",VERTEX,{"derivedFrom":[subQ0,sQuery(id+"F11.wireOp",EDGE,"E15.right")]}),1.0]])],"derivedFrom":subQ0})])],"isStart":false});}
            var Q10;
            Q10=makeQuery(id+"F12.opExtrude","CAP_EDGE",EDGE,{"disambiguationData":[OSD([sQuery(id+"F11.wireOp",EDGE,"E21")])],"isStart":false});
            var Q11;
            Q11=makeQuery(id+"F12.opExtrude","CAP_EDGE",EDGE,{"disambiguationData":[OSD([sQuery(id+"F11.wireOp",EDGE,"E20")])],"isStart":false});
            var Q12;
            Q12=makeQuery(id+"F12.opExtrude","CAP_EDGE",EDGE,{"disambiguationData":[OSD([sQuery(id+"F11.wireOp",EDGE,"E19")])],"isStart":false});
            var Q13;
            {var subQ0=sQuery(id+"F11.wireOp",EDGE,"E15.bottom");Q13=makeQuery(id+"F12.opExtrude","CAP_EDGE",EDGE,{"disambiguationData":[OSD([subQ0]),TDD([makeQuery(id+"F11.imprint","IMPRINT",EDGE,{"disambiguationData":[TD([[makeQuery(id+"F11.imprint","INTERSECT",VERTEX,{"derivedFrom":[subQ0,sQuery(id+"F11.wireOp",EDGE,"E18")]}),-1.0]])],"derivedFrom":subQ0})])],"isStart":false});}
            var Q14;
            Q14=makeQuery(id+"F12.opExtrude","CAP_EDGE",EDGE,{"disambiguationData":[OSD([sQuery(id+"F11.wireOp",EDGE,"E18")])],"isStart":false});
            var Q15;
            Q15=makeQuery(id+"F12.opExtrude","CAP_EDGE",EDGE,{"disambiguationData":[OSD([sQuery(id+"F11.wireOp",EDGE,"E17")])],"isStart":false});
            var Q16;
            Q16=makeQuery(id+"F12.opExtrude","CAP_EDGE",EDGE,{"disambiguationData":[OSD([sQuery(id+"F11.wireOp",EDGE,"E16")])],"isStart":false});
            var Q17;
            {var subQ0=sQuery(id+"F11.wireOp",EDGE,"E15.bottom");Q17=makeQuery(id+"F12.opExtrude","CAP_EDGE",EDGE,{"disambiguationData":[OSD([subQ0]),TDD([makeQuery(id+"F11.imprint","IMPRINT",EDGE,{"disambiguationData":[TD([[makeQuery(id+"F11.imprint","INTERSECT",VERTEX,{"derivedFrom":[subQ0,sQuery(id+"F11.wireOp",EDGE,"E15.left")]}),-1.0]])],"derivedFrom":subQ0})])],"isStart":false});}
            chamfer(context, id + "F23", {"entities" : qUnion([Q0, Q1, Q2, Q3, Q4, Q5, Q6, Q7, Q8, Q9, Q10, Q11, Q12, Q13, Q14, Q15, Q16, Q17]), "width" : (getVariable(context, 'c2')) * mm, "tangentPropagation" : true});
        }
        {
            var Q0;
            Q0=makeQuery(id+"F3.opExtrude","CAP_EDGE",EDGE,{"disambiguationData":[OSD([sQuery(id+"F2.wireOp",EDGE,"E2.top")])],"isStart":true});
            var Q1;
            Q1=makeQuery(id+"F10.opPattern","COPY",EDGE,{"derivedFrom":makeQuery(id+"F3.opExtrude","CAP_EDGE",EDGE,{"disambiguationData":[OSD([sQuery(id+"F2.wireOp",EDGE,"E2.top")])],"isStart":true}),"instanceName":"1"});
            var Q2;
            Q2=makeQuery(id+"F10.opPattern","COPY",EDGE,{"derivedFrom":makeQuery(id+"F3.opExtrude","CAP_EDGE",EDGE,{"disambiguationData":[OSD([sQuery(id+"F2.wireOp",EDGE,"E2.top")])],"isStart":true}),"instanceName":"2"});
            var Q3;
            Q3=makeQuery(id+"F10.opPattern","COPY",EDGE,{"derivedFrom":makeQuery(id+"F3.opExtrude","CAP_EDGE",EDGE,{"disambiguationData":[OSD([sQuery(id+"F2.wireOp",EDGE,"E2.top")])],"isStart":true}),"instanceName":"3"});
            var Q4;
            Q4=makeQuery(id+"F10.opPattern","COPY",EDGE,{"derivedFrom":makeQuery(id+"F3.opExtrude","CAP_EDGE",EDGE,{"disambiguationData":[OSD([sQuery(id+"F2.wireOp",EDGE,"E2.top")])],"isStart":true}),"instanceName":"4"});
            var Q5;
            Q5=makeQuery(id+"F10.opPattern","COPY",EDGE,{"derivedFrom":makeQuery(id+"F3.opExtrude","CAP_EDGE",EDGE,{"disambiguationData":[OSD([sQuery(id+"F2.wireOp",EDGE,"E2.top")])],"isStart":true}),"instanceName":"5"});
            var Q6;
            Q6=makeQuery(id+"F10.opPattern","COPY",EDGE,{"derivedFrom":makeQuery(id+"F3.opExtrude","CAP_EDGE",EDGE,{"disambiguationData":[OSD([sQuery(id+"F2.wireOp",EDGE,"E2.top")])],"isStart":false}),"instanceName":"4"});
            var Q7;
            Q7=makeQuery(id+"F10.opPattern","COPY",EDGE,{"derivedFrom":makeQuery(id+"F3.opExtrude","CAP_EDGE",EDGE,{"disambiguationData":[OSD([sQuery(id+"F2.wireOp",EDGE,"E2.top")])],"isStart":false}),"instanceName":"5"});
            var Q8;
            Q8=makeQuery(id+"F3.opExtrude","CAP_EDGE",EDGE,{"disambiguationData":[OSD([sQuery(id+"F2.wireOp",EDGE,"E2.top")])],"isStart":false});
            var Q9;
            Q9=makeQuery(id+"F10.opPattern","COPY",EDGE,{"derivedFrom":makeQuery(id+"F3.opExtrude","CAP_EDGE",EDGE,{"disambiguationData":[OSD([sQuery(id+"F2.wireOp",EDGE,"E2.top")])],"isStart":false}),"instanceName":"1"});
            var Q10;
            Q10=makeQuery(id+"F10.opPattern","COPY",EDGE,{"derivedFrom":makeQuery(id+"F3.opExtrude","CAP_EDGE",EDGE,{"disambiguationData":[OSD([sQuery(id+"F2.wireOp",EDGE,"E2.top")])],"isStart":false}),"instanceName":"2"});
            var Q11;
            Q11=makeQuery(id+"F10.opPattern","COPY",EDGE,{"derivedFrom":makeQuery(id+"F3.opExtrude","CAP_EDGE",EDGE,{"disambiguationData":[OSD([sQuery(id+"F2.wireOp",EDGE,"E2.top")])],"isStart":false}),"instanceName":"3"});
            var Q12;
            {var subQ0=sQuery(id+"F0.wireOp",EDGE,"E1");Q12=makeQuery(id+"F10.opPattern","COPY",EDGE,{"derivedFrom":makeQuery(id+"F7.boolean.opBoolean","INTERSECT",EDGE,{"derivedFrom":[makeQuery(id+"F3.boolean.opBoolean","MERGE",FACE,{"derivedFrom":[makeQuery(id+"F1.opExtrude","CAP_FACE",FACE,{"disambiguationData":[OSD([sQuery(id+"F0.wireOp",EDGE,"E0"),subQ0])],"isStart":false}),makeQuery(id+"F3.opExtrude","CAP_FACE",FACE,{"disambiguationData":[OSD([subQ0,sQuery(id+"F2.wireOp",EDGE,"E2.top"),sQuery(id+"F2.wireOp",EDGE,"E2.left"),sQuery(id+"F2.wireOp",EDGE,"E2.right")])],"isStart":false})]}),makeQuery(id+"F7.opExtrude","SWEPT_FACE",FACE,{"disambiguationData":[OSD([sQuery(id+"F6.wireOp",EDGE,"E12")])]})]}),"instanceName":"3"});}
            var Q13;
            {var subQ0=sQuery(id+"F0.wireOp",EDGE,"E1");Q13=makeQuery(id+"F10.opPattern","COPY",EDGE,{"derivedFrom":makeQuery(id+"F7.boolean.opBoolean","INTERSECT",EDGE,{"derivedFrom":[makeQuery(id+"F3.boolean.opBoolean","MERGE",FACE,{"derivedFrom":[makeQuery(id+"F1.opExtrude","CAP_FACE",FACE,{"disambiguationData":[OSD([sQuery(id+"F0.wireOp",EDGE,"E0"),subQ0])],"isStart":false}),makeQuery(id+"F3.opExtrude","CAP_FACE",FACE,{"disambiguationData":[OSD([subQ0,sQuery(id+"F2.wireOp",EDGE,"E2.top"),sQuery(id+"F2.wireOp",EDGE,"E2.left"),sQuery(id+"F2.wireOp",EDGE,"E2.right")])],"isStart":false})]}),makeQuery(id+"F7.opExtrude","SWEPT_FACE",FACE,{"disambiguationData":[OSD([sQuery(id+"F6.wireOp",EDGE,"E12")])]})]}),"instanceName":"2"});}
            var Q14;
            {var subQ0=sQuery(id+"F0.wireOp",EDGE,"E1");Q14=makeQuery(id+"F10.opPattern","COPY",EDGE,{"derivedFrom":makeQuery(id+"F7.boolean.opBoolean","INTERSECT",EDGE,{"derivedFrom":[makeQuery(id+"F3.boolean.opBoolean","MERGE",FACE,{"derivedFrom":[makeQuery(id+"F1.opExtrude","CAP_FACE",FACE,{"disambiguationData":[OSD([sQuery(id+"F0.wireOp",EDGE,"E0"),subQ0])],"isStart":false}),makeQuery(id+"F3.opExtrude","CAP_FACE",FACE,{"disambiguationData":[OSD([subQ0,sQuery(id+"F2.wireOp",EDGE,"E2.top"),sQuery(id+"F2.wireOp",EDGE,"E2.left"),sQuery(id+"F2.wireOp",EDGE,"E2.right")])],"isStart":false})]}),makeQuery(id+"F7.opExtrude","SWEPT_FACE",FACE,{"disambiguationData":[OSD([sQuery(id+"F6.wireOp",EDGE,"E12")])]})]}),"instanceName":"1"});}
            var Q15;
            {var subQ0=sQuery(id+"F0.wireOp",EDGE,"E1");Q15=makeQuery(id+"F7.boolean.opBoolean","INTERSECT",EDGE,{"derivedFrom":[makeQuery(id+"F3.boolean.opBoolean","MERGE",FACE,{"derivedFrom":[makeQuery(id+"F1.opExtrude","CAP_FACE",FACE,{"disambiguationData":[OSD([sQuery(id+"F0.wireOp",EDGE,"E0"),subQ0])],"isStart":false}),makeQuery(id+"F3.opExtrude","CAP_FACE",FACE,{"disambiguationData":[OSD([subQ0,sQuery(id+"F2.wireOp",EDGE,"E2.top"),sQuery(id+"F2.wireOp",EDGE,"E2.left"),sQuery(id+"F2.wireOp",EDGE,"E2.right")])],"isStart":false})]}),makeQuery(id+"F7.opExtrude","SWEPT_FACE",FACE,{"disambiguationData":[OSD([sQuery(id+"F6.wireOp",EDGE,"E12")])]})]});}
            var Q16;
            {var subQ0=sQuery(id+"F0.wireOp",EDGE,"E1");Q16=makeQuery(id+"F10.opPattern","COPY",EDGE,{"derivedFrom":makeQuery(id+"F7.boolean.opBoolean","INTERSECT",EDGE,{"derivedFrom":[makeQuery(id+"F3.boolean.opBoolean","MERGE",FACE,{"derivedFrom":[makeQuery(id+"F1.opExtrude","CAP_FACE",FACE,{"disambiguationData":[OSD([sQuery(id+"F0.wireOp",EDGE,"E0"),subQ0])],"isStart":false}),makeQuery(id+"F3.opExtrude","CAP_FACE",FACE,{"disambiguationData":[OSD([subQ0,sQuery(id+"F2.wireOp",EDGE,"E2.top"),sQuery(id+"F2.wireOp",EDGE,"E2.left"),sQuery(id+"F2.wireOp",EDGE,"E2.right")])],"isStart":false})]}),makeQuery(id+"F7.opExtrude","SWEPT_FACE",FACE,{"disambiguationData":[OSD([sQuery(id+"F6.wireOp",EDGE,"E12")])]})]}),"instanceName":"5"});}
            var Q17;
            {var subQ0=sQuery(id+"F0.wireOp",EDGE,"E1");Q17=makeQuery(id+"F10.opPattern","COPY",EDGE,{"derivedFrom":makeQuery(id+"F7.boolean.opBoolean","INTERSECT",EDGE,{"derivedFrom":[makeQuery(id+"F3.boolean.opBoolean","MERGE",FACE,{"derivedFrom":[makeQuery(id+"F1.opExtrude","CAP_FACE",FACE,{"disambiguationData":[OSD([sQuery(id+"F0.wireOp",EDGE,"E0"),subQ0])],"isStart":false}),makeQuery(id+"F3.opExtrude","CAP_FACE",FACE,{"disambiguationData":[OSD([subQ0,sQuery(id+"F2.wireOp",EDGE,"E2.top"),sQuery(id+"F2.wireOp",EDGE,"E2.left"),sQuery(id+"F2.wireOp",EDGE,"E2.right")])],"isStart":false})]}),makeQuery(id+"F7.opExtrude","SWEPT_FACE",FACE,{"disambiguationData":[OSD([sQuery(id+"F6.wireOp",EDGE,"E12")])]})]}),"instanceName":"4"});}
            var Q18;
            Q18=makeQuery(id+"F10.opPattern","COPY",EDGE,{"derivedFrom":makeQuery(id+"F7.boolean.opBoolean","COPY",EDGE,{"derivedFrom":makeQuery(id+"F7.opExtrude","CAP_EDGE",EDGE,{"disambiguationData":[OSD([sQuery(id+"F6.wireOp",EDGE,"E12")])],"isStart":true})}),"instanceName":"4"});
            var Q19;
            Q19=makeQuery(id+"F10.opPattern","COPY",EDGE,{"derivedFrom":makeQuery(id+"F7.boolean.opBoolean","COPY",EDGE,{"derivedFrom":makeQuery(id+"F7.opExtrude","CAP_EDGE",EDGE,{"disambiguationData":[OSD([sQuery(id+"F6.wireOp",EDGE,"E12")])],"isStart":true})}),"instanceName":"5"});
            var Q20;
            Q20=makeQuery(id+"F7.boolean.opBoolean","COPY",EDGE,{"derivedFrom":makeQuery(id+"F7.opExtrude","CAP_EDGE",EDGE,{"disambiguationData":[OSD([sQuery(id+"F6.wireOp",EDGE,"E12")])],"isStart":true})});
            var Q21;
            Q21=makeQuery(id+"F10.opPattern","COPY",EDGE,{"derivedFrom":makeQuery(id+"F7.boolean.opBoolean","COPY",EDGE,{"derivedFrom":makeQuery(id+"F7.opExtrude","CAP_EDGE",EDGE,{"disambiguationData":[OSD([sQuery(id+"F6.wireOp",EDGE,"E12")])],"isStart":true})}),"instanceName":"1"});
            var Q22;
            Q22=makeQuery(id+"F10.opPattern","COPY",EDGE,{"derivedFrom":makeQuery(id+"F7.boolean.opBoolean","COPY",EDGE,{"derivedFrom":makeQuery(id+"F7.opExtrude","CAP_EDGE",EDGE,{"disambiguationData":[OSD([sQuery(id+"F6.wireOp",EDGE,"E12")])],"isStart":true})}),"instanceName":"2"});
            var Q23;
            Q23=makeQuery(id+"F10.opPattern","COPY",EDGE,{"derivedFrom":makeQuery(id+"F7.boolean.opBoolean","COPY",EDGE,{"derivedFrom":makeQuery(id+"F7.opExtrude","CAP_EDGE",EDGE,{"disambiguationData":[OSD([sQuery(id+"F6.wireOp",EDGE,"E12")])],"isStart":true})}),"instanceName":"3"});
            chamfer(context, id + "F24", {"entities" : qUnion([Q0, Q1, Q2, Q3, Q4, Q5, Q6, Q7, Q8, Q9, Q10, Q11, Q12, Q13, Q14, Q15, Q16, Q17, Q18, Q19, Q20, Q21, Q22, Q23]), "width" : (getVariable(context, 'c2')) * mm, "tangentPropagation" : true});
        }
        {
            var Q0;
            {var subQ0=sQuery(id+"F11.wireOp",EDGE,"E15.right");var subQ1=sQuery(id+"F11.wireOp",EDGE,"E15.top");Q0=makeQuery(id+"F14.boolean.opBoolean","SPLIT",EDGE,{"disambiguationData":[TD([makeQuery(id+"F12.opExtrude","SWEPT_FACE",FACE,{"disambiguationData":[OSD([subQ0])]})])],"derivedFrom":makeQuery(id+"F12.opExtrude","CAP_EDGE",EDGE,{"disambiguationData":[OSD([subQ1])],"isStart":false})});}
            var Q1;
            {var subQ0=sQuery(id+"F11.wireOp",EDGE,"E15.left");var subQ1=sQuery(id+"F11.wireOp",EDGE,"E15.top");Q1=makeQuery(id+"F14.boolean.opBoolean","SPLIT",EDGE,{"disambiguationData":[TD([makeQuery(id+"F12.opExtrude","SWEPT_FACE",FACE,{"disambiguationData":[OSD([subQ0])]})])],"derivedFrom":makeQuery(id+"F12.opExtrude","CAP_EDGE",EDGE,{"disambiguationData":[OSD([subQ1])],"isStart":false})});}
            var Q2;
            {var subQ0=sQuery(id+"F11.wireOp",EDGE,"E15.right");var subQ1=sQuery(id+"F11.wireOp",EDGE,"E15.top");Q2=makeQuery(id+"F14.boolean.opBoolean","SPLIT",EDGE,{"disambiguationData":[TD([makeQuery(id+"F12.opExtrude","SWEPT_FACE",FACE,{"disambiguationData":[OSD([subQ0])]})])],"derivedFrom":makeQuery(id+"F12.opExtrude","CAP_EDGE",EDGE,{"disambiguationData":[OSD([subQ1])],"isStart":true})});}
            var Q3;
            {var subQ0=sQuery(id+"F11.wireOp",EDGE,"E15.left");var subQ1=sQuery(id+"F11.wireOp",EDGE,"E15.top");Q3=makeQuery(id+"F14.boolean.opBoolean","SPLIT",EDGE,{"disambiguationData":[TD([makeQuery(id+"F12.opExtrude","SWEPT_FACE",FACE,{"disambiguationData":[OSD([subQ0])]})])],"derivedFrom":makeQuery(id+"F12.opExtrude","CAP_EDGE",EDGE,{"disambiguationData":[OSD([subQ1])],"isStart":true})});}
            chamfer(context, id + "F25", {"entities" : qUnion([Q0, Q1, Q2, Q3]), "width" : 2 * mm, "tangentPropagation" : true});
        }
    });
